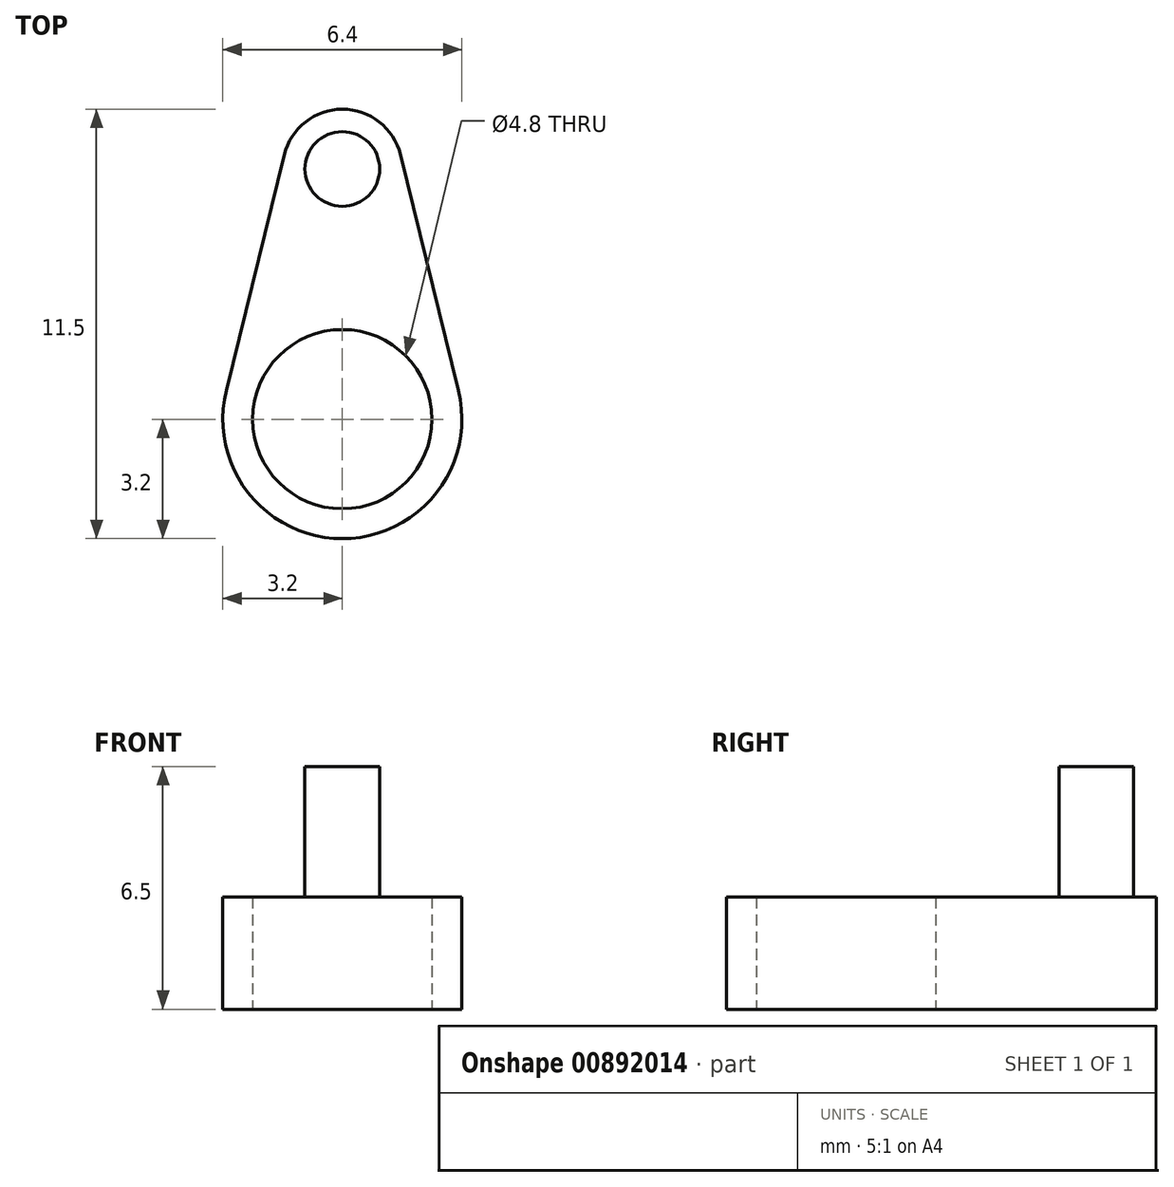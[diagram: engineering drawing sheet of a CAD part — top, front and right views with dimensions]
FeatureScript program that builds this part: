
annotation { "Feature Type Name" : "Feature", "Feature Type Description" : "" }
export const myFeature = defineFeature(function(context is Context, id is Id, definition is map)
    precondition{}
    {
        {
            var Q0;
            Q0=qCreatedBy(makeId("Top.planeOp"),FACE);
            var sketch = newSketch(context, id + "F0", { "sketchPlane" : qUnion([Q0])});
            skCircle(sketch, "E0", {"center": v(0, 0) * mm, "radius": 2.4 * mm});
            skCircle(sketch, "E1", {"center": v(0, 6.7) * mm, "radius": 1 * mm});
            skArc(sketch, "E2", {"start": v(1.55, 7.08) * mm, "mid": v(0, 8.3) * mm, "end": v(-1.55, 7.08) * mm});
            skArc(sketch, "E3", {"start": v(-3.1, 0.76) * mm, "mid": v(0, -3.2) * mm, "end": v(3.1, 0.76) * mm});
            skLineSegment(sketch, "E4", {"start": v(-1.55, 7.08) * mm, "end": v(-3.1, 0.76) * mm});
            skLineSegment(sketch, "E5.MirrorCS", {"start": v(1.55, 7.08) * mm, "end": v(3.1, 0.76) * mm});
            skArc(sketch, "E6", {"start": v(1.17, 5.53) * mm, "mid": v(1.52, 6.06) * mm, "end": v(1.65, 6.7) * mm});
            skLineSegment(sketch, "E7", {"start": v(0.35, 4.72) * mm, "end": v(1.17, 5.53) * mm});
            skLineSegment(sketch, "E8.trimOffspring", {"start": v(-1.17, 5.53) * mm, "end": v(-0.35, 4.72) * mm});
            skArc(sketch, "E9.trimOffspring", {"start": v(-1.65, 6.7) * mm, "mid": v(-1.52, 6.06) * mm, "end": v(-1.17, 5.53) * mm});
            skPoint(sketch, "E10.visualSharp", {"position": v(0, 4.37) * mm});
            skArc(sketch, "E10.filletArc", {"start": v(-0.35, 4.72) * mm, "mid": v(0, 4.57) * mm, "end": v(0.35, 4.72) * mm});
            skSolve(sketch);
        }
        {
            var Q0;
            Q0=makeQuery(id+"F0.imprint","IMPRINT",FACE,{"disambiguationData":[TD([[makeQuery(id+"F0.imprint","IMPRINT",EDGE,{"derivedFrom":sQuery(id+"F0.wireOp",EDGE,"E0")}),-1.0]])]});
            var Q1;
            Q1=makeQuery(id+"F0.imprint","IMPRINT",FACE,{"disambiguationData":[TD([[makeQuery(id+"F0.imprint","IMPRINT",EDGE,{"derivedFrom":sQuery(id+"F0.wireOp",EDGE,"E1")}),-1.0]])]});
            extrude(context, id + "F1", {"entities" : qUnion([Q0, Q1]), "depth" : 3 * mm, "offsetDistance" : 25 * mm});
        }
        {
            var Q0;
            Q0=makeQuery(id+"F0.imprint","IMPRINT",FACE,{"disambiguationData":[TD([[makeQuery(id+"F0.imprint","IMPRINT",EDGE,{"derivedFrom":sQuery(id+"F0.wireOp",EDGE,"E1")}),1.0]])]});
            extrude(context, id + "F2", {"entities" : qUnion([Q0]), "operationType" : NewBodyOperationType.ADD, "depth" : 6.5 * mm, "offsetDistance" : 25 * mm});
        }
    });
